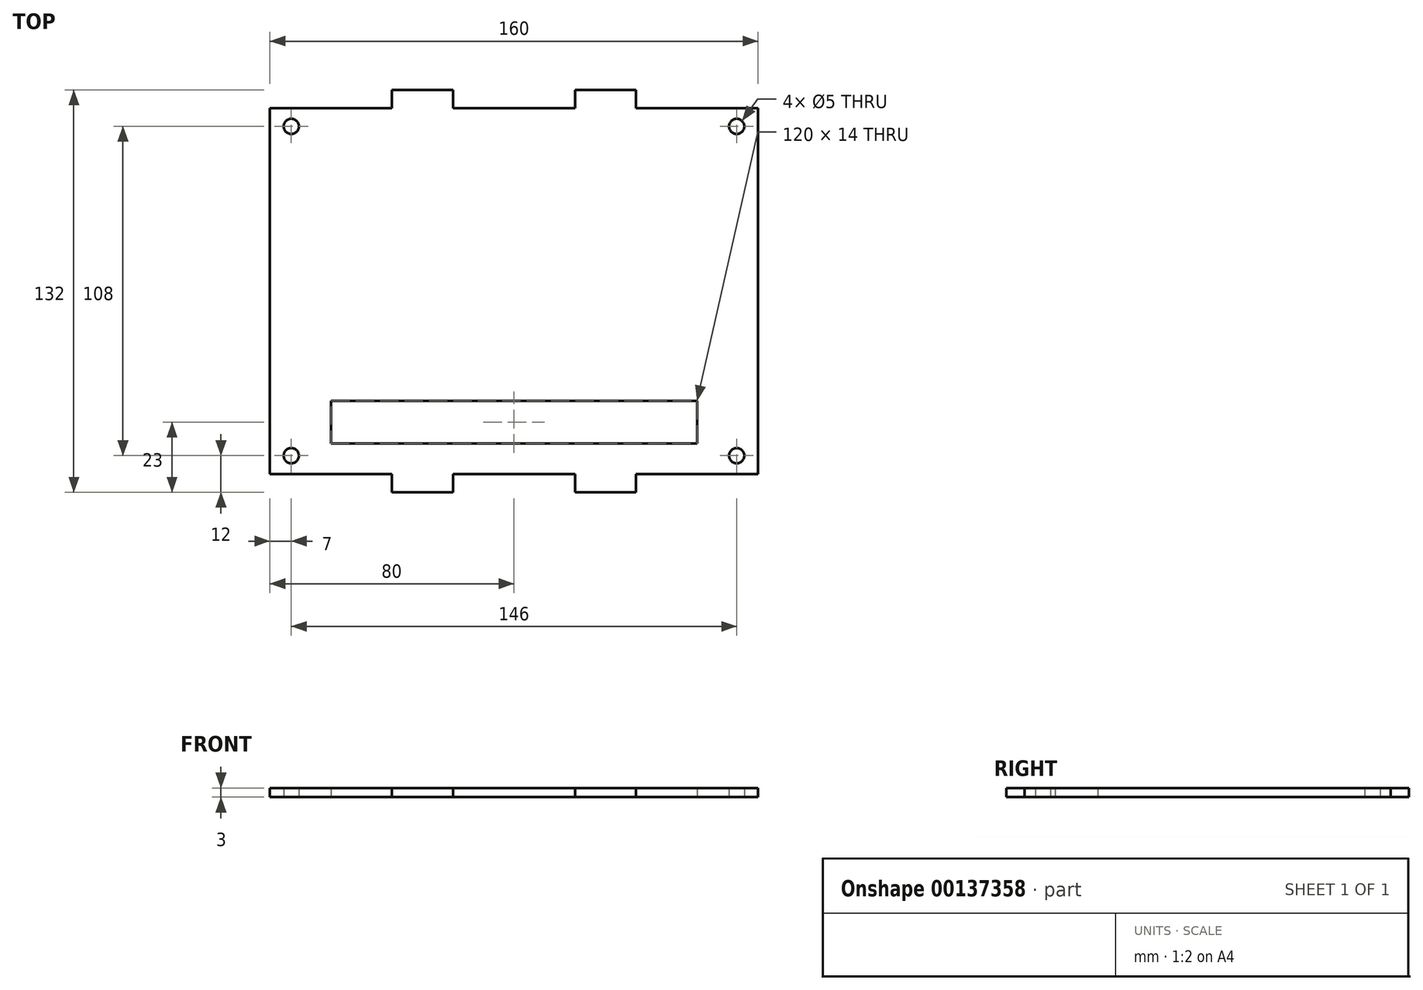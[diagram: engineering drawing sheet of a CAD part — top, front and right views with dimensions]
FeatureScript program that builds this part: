
annotation { "Feature Type Name" : "Feature", "Feature Type Description" : "" }
export const myFeature = defineFeature(function(context is Context, id is Id, definition is map)
    precondition{}
    {
        {
            var Q0;
            Q0=qCreatedBy(makeId("Top.planeOp"),FACE);
            var sketch = newSketch(context, id + "F0", { "sketchPlane" : qUnion([Q0])});
            skLineSegment(sketch, "E0.bottom", {"start": v(80, 60) * mm, "end": v(40, 60) * mm});
            skLineSegment(sketch, "E0.top", {"start": v(80, -60) * mm, "end": v(40, -60) * mm});
            skLineSegment(sketch, "E0.left", {"start": v(80, 60) * mm, "end": v(80, -60) * mm});
            skLineSegment(sketch, "E0.right", {"start": v(-80, 60) * mm, "end": v(-80, -60) * mm});
            skPoint(sketch, "E0.middle", {"position": v(0, 0) * mm});
            skLineSegment(sketch, "E1", {"start": v(0, 0) * mm, "end": v(0, -60) * mm, "construction": true});
            skLineSegment(sketch, "E2", {"start": v(0, -60) * mm, "end": v(0, -50) * mm, "construction": true});
            skLineSegment(sketch, "E3", {"start": v(0, -50) * mm, "end": v(60, -50) * mm, "construction": true});
            skLineSegment(sketch, "E4", {"start": v(-80, 0) * mm, "end": v(80, 0) * mm, "construction": true});
            skLineSegment(sketch, "E5", {"start": v(-80, -60) * mm, "end": v(-73, -60) * mm, "construction": true});
            skLineSegment(sketch, "E6", {"start": v(-73, -60) * mm, "end": v(-73, -54) * mm, "construction": true});
            skCircle(sketch, "E7", {"center": v(-73, -54) * mm, "radius": 2.5 * mm});
            skCircle(sketch, "E8.MirrorC", {"center": v(73, -54) * mm, "radius": 2.5 * mm});
            skCircle(sketch, "E9.MirrorC", {"center": v(-73, 54) * mm, "radius": 2.5 * mm});
            skCircle(sketch, "E10.MirrorC", {"center": v(73, 54) * mm, "radius": 2.5 * mm});
            skLineSegment(sketch, "E11", {"start": v(0, -50) * mm, "end": v(-60, -50) * mm});
            skLineSegment(sketch, "E12", {"start": v(-60, -50) * mm, "end": v(-60, -36) * mm});
            skLineSegment(sketch, "E13", {"start": v(-60, -36) * mm, "end": v(60, -36) * mm});
            skLineSegment(sketch, "E14", {"start": v(60, -36) * mm, "end": v(60, -50) * mm});
            skLineSegment(sketch, "E15", {"start": v(0, -50) * mm, "end": v(60, -50) * mm});
            skLineSegment(sketch, "E16", {"start": v(0, 60) * mm, "end": v(-20, 60) * mm, "construction": true});
            skLineSegment(sketch, "E17", {"start": v(-20, 60) * mm, "end": v(-20, 66) * mm});
            skLineSegment(sketch, "E18", {"start": v(-20, 66) * mm, "end": v(-40, 66) * mm});
            skLineSegment(sketch, "E19", {"start": v(-40, 66) * mm, "end": v(-40, 60) * mm});
            skLineSegment(sketch, "E20", {"start": v(0, 60) * mm, "end": v(20, 60) * mm, "construction": true});
            skLineSegment(sketch, "E21", {"start": v(20, 60) * mm, "end": v(20, 66) * mm});
            skLineSegment(sketch, "E22", {"start": v(20, 66) * mm, "end": v(40, 66) * mm});
            skLineSegment(sketch, "E23", {"start": v(40, 66) * mm, "end": v(40, 60) * mm});
            skLineSegment(sketch, "E24.trimOffspring", {"start": v(-40, 60) * mm, "end": v(-80, 60) * mm});
            skLineSegment(sketch, "E25.trimOffspring", {"start": v(20, 60) * mm, "end": v(-20, 60) * mm});
            skLineSegment(sketch, "E26.MirrorCS", {"start": v(0, -60) * mm, "end": v(-20, -60) * mm, "construction": true});
            skLineSegment(sketch, "E27.MirrorCS", {"start": v(0, -60) * mm, "end": v(20, -60) * mm, "construction": true});
            skLineSegment(sketch, "E28", {"start": v(-20, -60) * mm, "end": v(-20, -66) * mm});
            skLineSegment(sketch, "E29", {"start": v(-20, -66) * mm, "end": v(-40, -66) * mm});
            skLineSegment(sketch, "E30", {"start": v(-40, -66) * mm, "end": v(-40, -60) * mm});
            skLineSegment(sketch, "E31", {"start": v(20, -60) * mm, "end": v(20, -66) * mm});
            skLineSegment(sketch, "E32", {"start": v(20, -66) * mm, "end": v(40, -66) * mm});
            skLineSegment(sketch, "E33", {"start": v(40, -66) * mm, "end": v(40, -60) * mm});
            skLineSegment(sketch, "E34.trimOffspring", {"start": v(-40, -60) * mm, "end": v(-80, -60) * mm});
            skLineSegment(sketch, "E35.trimOffspring", {"start": v(20, -60) * mm, "end": v(-20, -60) * mm});
            skSolve(sketch);
        }
        {
            var Q0;
            Q0=makeQuery(id+"F0.imprint","IMPRINT",FACE,{"disambiguationData":[TD([[makeQuery(id+"F0.imprint","IMPRINT",EDGE,{"derivedFrom":sQuery(id+"F0.wireOp",EDGE,"E0.bottom")}),1.0]])]});
            extrude(context, id + "F1", {"entities" : qUnion([Q0]), "endBound" : BoundingType.SYMMETRIC, "depth" : 3 * mm});
        }
    });
